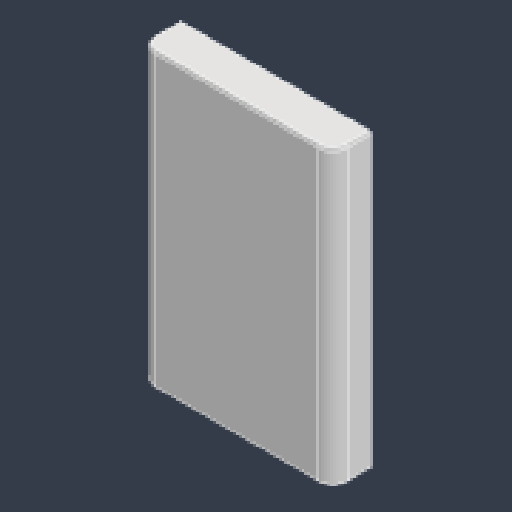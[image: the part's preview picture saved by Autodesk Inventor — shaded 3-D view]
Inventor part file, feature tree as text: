
AUTODESK INVENTOR PART (.ipt)
format: ipt  version: 2023.4 (Build 274418000, 418)  size: 100,352 bytes
history: native  units: mm
features: fillet x2, extrude x1, sketch x1
ambient origin geometry x8: Origin, YZ Plane, XZ Plane, XY Plane, X Axis, Y Axis, Z Axis, Center Point
bodies: Solid1 (feature_tree)
feature tree (4):
  extrude  "Extrusion1"  Depth=60.5mm
  fillet  "Fillet1"  Radius=8.0mm
  fillet  "Fillet2"  Radius=3.0mm
  sketch  "Sketch1"  dims[d0=39.8mm d1=60.5mm d2=8.0mm d3=0.0mm d4=3.0mm d5=0.5mm]
